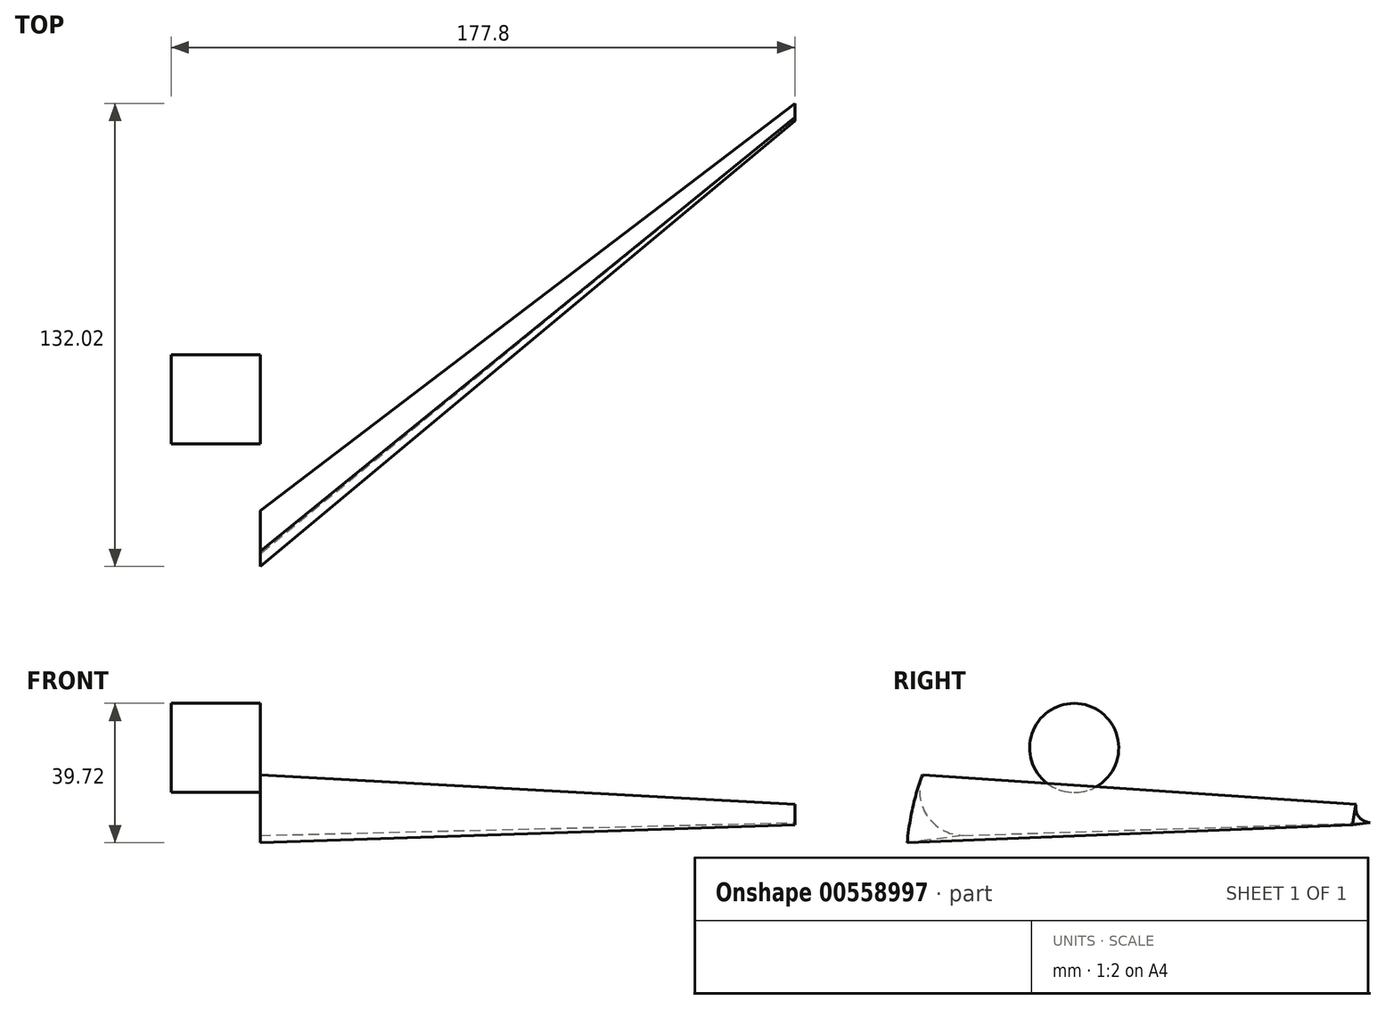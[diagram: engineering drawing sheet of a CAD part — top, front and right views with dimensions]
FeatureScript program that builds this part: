
annotation { "Feature Type Name" : "Feature", "Feature Type Description" : "" }
export const myFeature = defineFeature(function(context is Context, id is Id, definition is map)
    precondition{}
    {
        {
            var Q0;
            Q0=qCreatedBy(makeId("Right.planeOp"),FACE);
            cPlane(context, id + "F0", {"entities" : qUnion([Q0]), "cplaneType" : CPlaneType.OFFSET, "offset" : 25.4 * mm, "width" : 152.4 * mm, "height" : 152.4 * mm});
        }
        {
            var Q0;
            Q0=qCreatedBy(id+"F0.planeOp",FACE);
            var sketch = newSketch(context, id + "F1", { "sketchPlane" : qUnion([Q0])});
            skPoint(sketch, "E0", {"position": v(0, 0) * mm});
            skPoint(sketch, "E1", {"position": v(355.6, 0) * mm});
            skPoint(sketch, "E2", {"position": v(254, 5.55) * mm});
            skPoint(sketch, "E3", {"position": v(254, 25.4) * mm});
            skPoint(sketch, "E4", {"position": v(50.8, 50.8) * mm});
            skFitSpline(sketch, "E5", {"points": [v(0, 0) * mm, v(50.8, 50.8) * mm, v(254, 25.4) * mm, v(355.6, 0) * mm, v(254, 5.55) * mm], "startDerivative": vector(54.3, 516.72) * mm, "endDerivative": vector(-643.37, 57.95) * mm});
            skFitSpline(sketch, "E6", {"points": [v(254, 5.55) * mm, v(0, 0) * mm], "startDerivative": vector(-151.2, 19.05) * mm, "endDerivative": vector(-291.33, -38.1) * mm});
            skLineSegment(sketch, "E7", {"start": v(3.56, 33.87) * mm, "end": v(0, 0) * mm});
            skLineSegment(sketch, "E8", {"start": v(0, 0) * mm, "end": v(0, 76.62) * mm});
            skLineSegment(sketch, "E9", {"start": v(97.11, 12.7) * mm, "end": v(0, 0) * mm});
            skArc(sketch, "E10.filletArc", {"start": v(4.42, 19.38) * mm, "mid": v(6.2, 7.03) * mm, "end": v(17.68, 2.16) * mm});
            skLineSegment(sketch, "E11", {"start": v(203.6, 11.9) * mm, "end": v(254, 5.55) * mm});
            skSolve(sketch);
        }
        {
            var Q0;
            Q0=qCreatedBy(makeId("Right.planeOp"),FACE);
            cPlane(context, id + "F2", {"entities" : qUnion([Q0]), "cplaneType" : CPlaneType.OFFSET, "offset" : 177.8 * mm, "width" : 152.4 * mm, "height" : 152.4 * mm});
        }
        {
            var Q0;
            Q0=qCreatedBy(id+"F2.planeOp",FACE);
            var sketch = newSketch(context, id + "F3", { "sketchPlane" : qUnion([Q0])});
            skPoint(sketch, "E12", {"position": v(127, 5.08) * mm});
            skPoint(sketch, "E13", {"position": v(152.4, 30.48) * mm});
            skPoint(sketch, "E14", {"position": v(254, 17.78) * mm});
            skPoint(sketch, "E15", {"position": v(304.8, 5.08) * mm});
            skPoint(sketch, "E16", {"position": v(254, 11.43) * mm});
            skFitSpline(sketch, "E17", {"points": [v(127, 5.08) * mm, v(152.4, 30.48) * mm, v(254, 17.78) * mm, v(304.8, 5.08) * mm, v(254, 11.43) * mm], "startDerivative": vector(27.17, 258.55) * mm, "endDerivative": vector(-321.25, 46.07) * mm});
            skFitSpline(sketch, "E18", {"points": [v(254, 11.43) * mm, v(127, 5.08) * mm], "startDerivative": vector(-50.4, 6.35) * mm, "endDerivative": vector(-97.11, -12.7) * mm});
            skLineSegment(sketch, "E19", {"start": v(127, 5.08) * mm, "end": v(127, 20) * mm});
            skLineSegment(sketch, "E20", {"start": v(128.78, 22.01) * mm, "end": v(127, 5.08) * mm});
            skLineSegment(sketch, "E21", {"start": v(127, 5.08) * mm, "end": v(159.37, 9.31) * mm});
            skLineSegment(sketch, "E22", {"start": v(254, 11.43) * mm, "end": v(254, 15.33) * mm});
            skLineSegment(sketch, "E23", {"start": v(237.2, 13.55) * mm, "end": v(254, 11.43) * mm});
            skArc(sketch, "E24.filletArc", {"start": v(128.02, 11) * mm, "mid": v(128.94, 7.18) * mm, "end": v(132.6, 5.76) * mm});
            skSolve(sketch);
        }
        {
            var Q0;
            {var subQ0=sQuery(id+"F1.wireOp",EDGE,"E5");Q0=makeQuery(id+"F1.imprint","IMPRINT",FACE,{"disambiguationData":[TD([[makeQuery(id+"F1.imprint","IMPRINT",EDGE,{"derivedFrom":subQ0}),-1.0]])]});}
            var Q1;
            {var subQ0=sQuery(id+"F3.wireOp",EDGE,"E17");Q1=makeQuery(id+"F3.imprint","IMPRINT",FACE,{"disambiguationData":[TD([[makeQuery(id+"F3.imprint","IMPRINT",EDGE,{"derivedFrom":subQ0}),-1.0]])]});}
            loft(context, id + "F4", {"sheetProfilesArray" : [{ "sheetProfileEntities" : qUnion([Q0]) }, { "sheetProfileEntities" : qUnion([Q1]) }]});
        }
        {
            var Q0;
            {var subQ0=sQuery(id+"F1.wireOp",EDGE,"E5");Q0=makeQuery(id+"F4.opLoft","CAP_FACE",FACE,{"disambiguationData":[OSD([makeQuery(id+"F1.imprint","IMPRINT",FACE,{"disambiguationData":[TD([[makeQuery(id+"F1.imprint","IMPRINT",EDGE,{"derivedFrom":subQ0}),-1.0]])]})])],"isStart":true});}
            var sketch = newSketch(context, id + "F5", { "sketchPlane" : qUnion([Q0])});
            skPoint(sketch, "E25", {"position": v(-47.62, 27.02) * mm});
            skCircle(sketch, "E26", {"center": v(-47.62, 27.02) * mm, "radius": 12.7 * mm});
            skSolve(sketch);
        }
        {
            var Q0;
            Q0=makeQuery(id+"F5.imprint","IMPRINT",FACE,{"disambiguationData":[TD([[makeQuery(id+"F5.imprint","IMPRINT",EDGE,{"derivedFrom":sQuery(id+"F5.wireOp",EDGE,"E26")}),1.0]])]});
            extrude(context, id + "F6", {"entities" : qUnion([Q0]), "operationType" : NewBodyOperationType.ADD, "depth" : 25.4 * mm, "offsetDistance" : 25.4 * mm});
        }
    });
